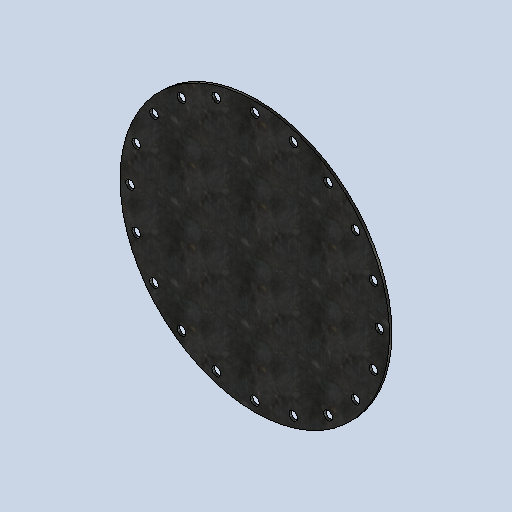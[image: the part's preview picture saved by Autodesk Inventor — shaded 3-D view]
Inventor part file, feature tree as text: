
AUTODESK INVENTOR PART (.ipt)
format: ipt  version: 2025.1 (Build 291241020, 241B)  size: 258,048 bytes
history: native  units: mm
features: sketch x2, other x2, extrude x1, pattern_circular x1
ambient origin geometry x8: Origin, YZ Plane, XZ Plane, XY Plane, X Axis, Y Axis, Z Axis, Center Point
bodies: Solid1 (feature_tree)
feature tree (6):
  extrude  "Extrusion1"  Depth=6.0mm TaperAngle=0.0deg
  pattern_circular  "Circular Pattern1"  Count=62  [1 undecoded]
  sketch  "Sketch1"  dims[d0=670.0mm d1=6.0mm d2=0.0mm]
  sketch  "Sketch2"  dims[d3=22.0mm d4=620.0mm d5=6.0mm d6=6.0mm d7=0.0mm d8=200.0mm d9=360.0deg]
  other  "Cut1"
  other  "Definition1"
note: 1 required parameter value undecoded (feature->parameter linkage not recoverable at this tier; creation-order binding heuristic only, values carry confidence <= 0.55)
